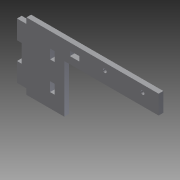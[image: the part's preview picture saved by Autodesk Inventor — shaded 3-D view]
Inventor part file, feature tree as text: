
AUTODESK INVENTOR PART (.ipt)
format: ipt  version: 2011 (Build 150239000, 239)  size: 205,824 bytes
history: native  units: in
note: dims shown in document units (in); Inventor stores cm internally (conversion verified against a paired STEP export)
features: extrude x7, sketch x7
ambient origin geometry x8: Origin, YZ Plane, XZ Plane, XY Plane, X Axis, Y Axis, Z Axis, Center Point
bodies: Solid1 (feature_tree)
feature tree (14):
  extrude  "Extrusion1"  Depth=1.0in
  extrude  "Extrusion2"  Depth=3.55in
  extrude  "Extrusion3"  Depth=1.0in
  extrude  "Extrusion4"  Depth=0.85in
  extrude  "Extrusion5"  Depth=2.0in
  extrude  "Extrusion6"  Depth=0.196in
  extrude  "Extrusion7"  Depth=0.75in
  sketch  "Sketch2"  dims[d5=7.25in d6=1.0in]
  sketch  "Sketch3"  dims[d7=5.0in d8=3.55in]
  sketch  "Sketch4"  dims[d9=0.25in d10=1.0in]
  sketch  "Sketch5"  dims[d11=1.0in d12=0.85in]
  sketch  "Sketch6"  dims[d13=0.375in d14=2.0in]
  sketch  "Sketch7"  dims[d15=0.196in d16=0.196in]
  sketch  "Sketch8"  dims[d17=0.75in d18=0.75in d19=0.5in d20=0.25in d21=1.0in d22=0.25in d23=0.5in d24=0.25in d25=0.0in d26=0.5in d27=0.25in d28=0.5in d29=0.25in d30=1.0in d31=0.0in d32=0.3in d33=0.5in d34=1.0in d35=0.3in d36=0.5in d37=1.0in d38=1.0in d39=0.0in d40=0.1in d41=0.1in d42=1.0in d43=0.0in d44=4.0in d45=1.0in d46=0.0in d47=0.25in d48=0.0in d49=3.7in d50=0.625in d51=0.25in d52=0.5in d53=0.5in d54=1.0in d55=0.0in]
